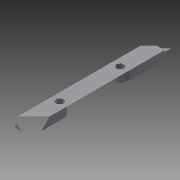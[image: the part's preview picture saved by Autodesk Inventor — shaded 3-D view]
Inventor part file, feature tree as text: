
AUTODESK INVENTOR PART (.ipt)
format: ipt  version: 2015 (Build 190159000, 159)  size: 198,656 bytes
history: native  units: in
note: dims shown in document units (in); Inventor stores cm internally (conversion verified against a paired STEP export)
features: extrude x7, sketch x7, projected_geometry x7, reference x2, chamfer x1, fillet x1
ambient origin geometry x8: Origin, YZ Plane, XZ Plane, XY Plane, X Axis, Y Axis, Z Axis, Center Point
bodies: Solid1 (feature_tree)
feature tree (25):
  extrude  "Extrusion1"  Depth=1.0in
  extrude  "Extrusion2"  Depth=0.25in
  extrude  "Extrusion3"  Depth=4.8in TaperAngle=0.0deg
  extrude  "Extrusion4"  Depth=0.1in TaperAngle=0.0deg
  chamfer  "Chamfer1"  Distance=0.0625in
  fillet  "Fillet1"  Radius=0.375in
  extrude  "Extrusion6"  Depth=0.3in TaperAngle=0.0deg
  extrude  "Extrusion5"  Depth=0.1875in
  extrude  "Extrusion7"  Depth=0.1875in TaperAngle=0.0deg
  sketch  "Sketch1"  dims[d0=1.0in d1=0.25in]
  sketch  "Sketch2"  dims[d2=9.3625in d3=0.0in d6=0.25in]
  projected_geometry  "Projected Loop1"
  sketch  "Sketch3"  dims[d7=0.25in d8=4.8in d9=0.0in]
  reference  "Reference1"
  reference  "Reference2"
  projected_geometry  "Projected Loop2"
  sketch  "Sketch5"  dims[d10=3.8in d11=0.1in d12=0.0in d13=0.0625in d14=0.0in]
  projected_geometry  "Projected Loop4"
  sketch  "Sketch6"  dims[d15=0.25in d16=0.9375in d17=45.0deg d18=0.375in]
  projected_geometry  "Projected Loop5"
  sketch  "Sketch8"  dims[d19=0.4375in d20=0.3in d21=0.0in]
  projected_geometry  "Projected Loop6"
  sketch  "Sketch9"  dims[d22=0.6562in d23=0.0in d24=0.624in d25=0.1875in d26=0.0in]
  projected_geometry  "Projected Loop7"
  projected_geometry  "Projected Loop8"
